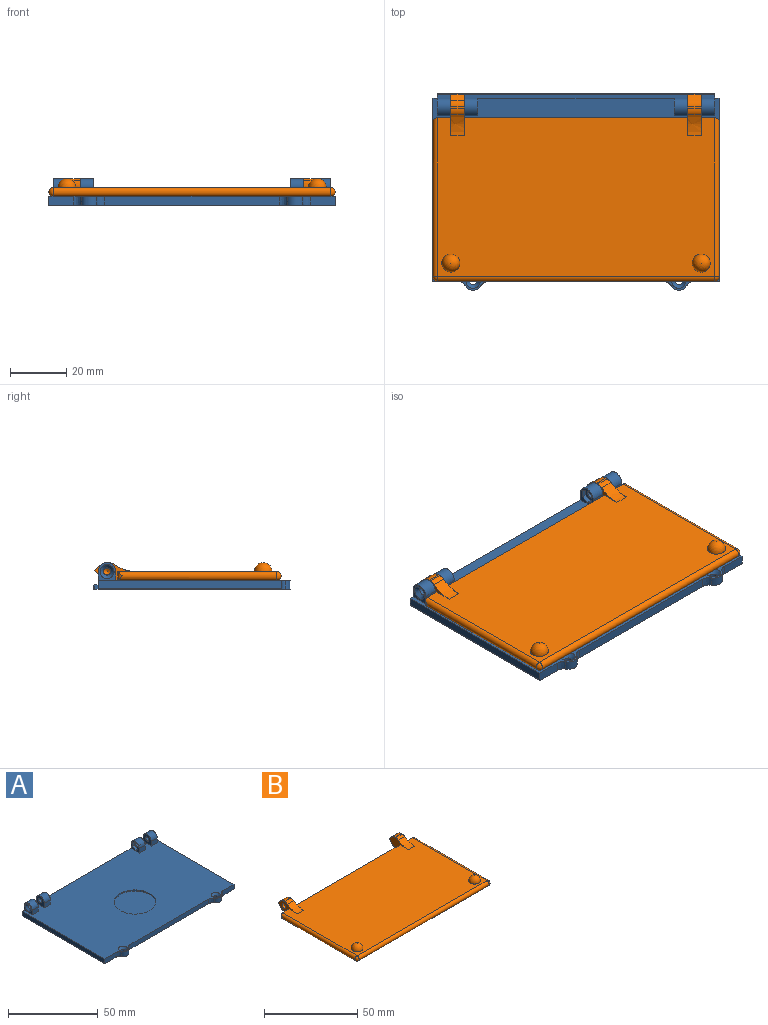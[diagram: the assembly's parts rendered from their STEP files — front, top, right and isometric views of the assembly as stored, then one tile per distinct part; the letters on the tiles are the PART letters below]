
ASSEMBLY  parts=2 mates=1
PART A: 66 faces, bbox 102x70.2x10.1 mm
  f0: plane 6.35x6.35mm, normal (-1,0,0), area 16.2mm2, adj f2,f11,f39,f41,f51,f52,f53,f54
  f1: plane 6.35x6.35mm, normal (1,0,0), area 16.2mm2, adj f2,f11,f34,f42,f44,f45,f46,f47
  f2: plane 101.97x68.62mm, normal (0,0,1), area 6061.6mm2, adj f0,f1,f3,f4,f5,f9,f10,f11
  f3: plane 8.8x3.18mm, normal (0,-1,0), area 27.9mm2, adj f2,f5,f8,f17,f29
  f4: plane 62x3.18mm, normal (0,-1,0), area 196.9mm2, adj f2,f8,f16,f18
  f5: plane 65.08x2.92mm, normal (1,0,0), area 190.1mm2, adj f2,f3,f11,f29
  f6: plane 97.94x1.09mm, normal (0,1,0), area 107mm2, adj f24,f25,f26,f27
  f7: plane 98.45x1.32mm, normal (0,0,1), area 130mm2, adj f11,f12,f13,f26
  f8: plane 101.46x69.94mm, normal (0,0,-1), area 6733.1mm2, adj f3,f4,f9,f11,f12,f13,f14,f15
  f9: plane 8.8x3.18mm, normal (0,-1,0), area 27.9mm2, adj f2,f8,f10,f19,f28
  f10: plane 65.08x2.92mm, normal (-1,0,0), area 190.1mm2, adj f2,f9,f11,f28
  f11: plane 101.6x6.35mm, normal (0,1,0), area 225.5mm2, adj f0,f1,f2,f5,f7,f8,f10,f12
  f12: plane 1.6x1.32mm, normal (1,0,0), area 2.1mm2, adj f7,f8,f11,f27
  f13: plane 1.6x1.32mm, normal (-1,0,0), area 2.1mm2, adj f7,f8,f11,f24
  f14: cylinder r=3.17mm len=5.5mm, axis (0,0,1), area 21.1mm2, adj f2,f8,f16,f17
  f15: cylinder r=3.17mm len=5.5mm, axis (0,0,-1), area 21.1mm2, adj f2,f8,f18,f19
  f16: bspline ~3.49x2.75mm, area 10.6mm2, adj f2,f4,f8,f14
  f17: bspline ~3.49x2.75mm, area 10.6mm2, adj f2,f3,f8,f14
  f18: bspline ~3.49x2.75mm, area 10.6mm2, adj f2,f4,f8,f15
  f19: bspline ~3.49x2.75mm, area 10.6mm2, adj f2,f8,f9,f15
  f20: cylinder r=1.27mm len=2.54mm, axis (0,0,1), area 14.2mm2, adj f8,f22
  f21: cylinder r=1.27mm len=2.54mm, axis (0,0,1), area 14.2mm2, adj f8,f23
  f22: cone r=1.27mm half-angle=41deg, axis (0,0,1), area 21.8mm2, adj f2,f20
  f23: cone r=1.27mm half-angle=41deg, axis (0,0,1), area 21.8mm2, adj f2,f21
  f24: cylinder r=0.25mm len=1.6mm, axis (0,0,-1), area 0.5mm2, adj f6,f13,f25,f26
  f25: cylinder r=0.25mm len=98.45mm, axis (1,0,0), area 39.2mm2, adj f6,f8,f24,f27
  f26: cylinder r=0.25mm len=98.45mm, axis (-1,0,0), area 39.2mm2, adj f6,f7,f24,f27
  f27: cylinder r=0.25mm len=1.6mm, axis (0,0,1), area 0.5mm2, adj f6,f12,f25,f26
  f28: cylinder r=0.25mm len=65.08mm, axis (0,1,0), area 26mm2, adj f8,f9,f10,f11
  f29: cylinder r=0.25mm len=65.08mm, axis (0,-1,0), area 26mm2, adj f3,f5,f8,f11
  f30: plane 6.35x6.35mm, normal (-1,0,0), area 16.6mm2, adj f2,f11,f31,f43,f63
  f31: plane 4.76x3.18mm, normal (0,-1,0), area 15.1mm2, adj f2,f30,f32,f43
  f32: plane 6.35x6.35mm, normal (1,0,0), area 30.9mm2, adj f2,f11,f31,f43,f61
  f33: plane 6.35x6.35mm, normal (-1,0,0), area 30.9mm2, adj f2,f11,f34,f42,f59
  f34: plane 4.76x3.18mm, normal (0,-1,0), area 15.1mm2, adj f1,f2,f33,f42
  f35: plane 6.35x6.35mm, normal (1,0,0), area 16.6mm2, adj f2,f11,f37,f40,f62
  f36: plane 6.35x6.35mm, normal (-1,0,0), area 30.9mm2, adj f2,f11,f37,f40,f60
  f37: plane 4.76x3.18mm, normal (0,-1,0), area 15.1mm2, adj f2,f35,f36,f40
  f38: plane 6.35x6.35mm, normal (1,0,0), area 30.9mm2, adj f2,f11,f39,f41,f58
  f39: plane 4.76x3.18mm, normal (0,-1,0), area 15.1mm2, adj f0,f2,f38,f41
  f40: cylinder r=3.17mm len=6.35mm, axis (-1,0,0), area 47.5mm2, adj f11,f35,f36,f37
  f41: cylinder r=3.17mm len=6.35mm, axis (-1,0,0), area 47.5mm2, adj f0,f11,f38,f39
  f42: cylinder r=3.17mm len=6.35mm, axis (-1,0,0), area 47.5mm2, adj f1,f11,f33,f34
  f43: cylinder r=3.17mm len=6.35mm, axis (-1,0,0), area 47.5mm2, adj f11,f30,f31,f32
  f44: plane 2.39x1.6mm, normal (0,0.5,-0.87), area 4.4mm2, adj f1,f45,f49,f50
  f45: plane 2.76x1.6mm, normal (0,1,0), area 4.4mm2, adj f1,f44,f46,f50
  f46: plane 2.39x1.6mm, normal (0,0.5,0.87), area 4.4mm2, adj f1,f45,f47,f50
  f47: plane 2.39x1.6mm, normal (0,-0.5,0.87), area 4.4mm2, adj f1,f46,f48,f50
  f48: plane 2.76x1.6mm, normal (0,-1,0), area 4.4mm2, adj f1,f47,f49,f50
  f49: plane 2.39x1.6mm, normal (0,-0.5,-0.87), area 4.4mm2, adj f1,f44,f48,f50
  f50: plane 5.51x4.78mm, normal (1,0,0), area 14.7mm2, adj f44,f45,f46,f47,f48,f49,f59
  f51: plane 2.39x1.59mm, normal (0,-0.5,-0.87), area 4.4mm2, adj f0,f52,f56,f57
  f52: plane 2.76x1.59mm, normal (0,-1,0), area 4.4mm2, adj f0,f51,f53,f57
  f53: plane 2.39x1.59mm, normal (0,-0.5,0.87), area 4.4mm2, adj f0,f52,f54,f57
  f54: plane 2.39x1.59mm, normal (0,0.5,0.87), area 4.4mm2, adj f0,f53,f55,f57
  f55: plane 2.76x1.59mm, normal (0,1,0), area 4.4mm2, adj f0,f54,f56,f57
  f56: plane 2.39x1.59mm, normal (0,0.5,-0.87), area 4.4mm2, adj f0,f51,f55,f57
  f57: plane 5.51x4.78mm, normal (-1,0,0), area 14.7mm2, adj f51,f52,f53,f54,f55,f56,f58
  f58: cylinder r=1.27mm len=3.18mm, axis (-1,0,0), area 25.3mm2, adj f38,f57
  f59: cylinder r=1.27mm len=3.16mm, axis (1,0,0), area 25.2mm2, adj f33,f50
  f60: cylinder r=1.27mm len=3.37mm, axis (1,0,0), area 26.9mm2, adj f36,f62
  f61: cylinder r=1.27mm len=3.37mm, axis (-1,0,0), area 26.9mm2, adj f32,f63
  f62: cone r=1.27mm half-angle=41deg, axis (1,0,0), area 21.8mm2, adj f35,f60
  f63: cone r=1.27mm half-angle=41deg, axis (-1,0,0), area 21.8mm2, adj f30,f61
  f64: cylinder r=11.63mm len=23.26mm, axis (0,0,1), area 57.9mm2, adj f2,f65
  f65: plane 23.26x23.26mm, normal (0,0,1), area 425mm2, adj f64
PART B: 36 faces, bbox 102.7x67.3x7.5 mm
  f0: cylinder r=3.17mm len=4.78mm, axis (-1,0,0), area 13.2mm2, adj f6,f9,f10,f22
  f1: cylinder r=3.17mm len=4.78mm, axis (-1,0,0), area 11.4mm2, adj f12,f13,f14,f19
  f2: plane 4.76x3.18mm, normal (0,1,0), area 15.1mm2, adj f5,f6,f13,f32
  f3: plane 79.35x3.18mm, normal (0,1,0), area 251.9mm2, adj f5,f6,f10,f12
  f4: plane 4.76x3.18mm, normal (0,1,0), area 15.1mm2, adj f5,f6,f9,f29
  f5: plane 98.43x56.36mm, normal (0,0,1), area 5422.8mm2, adj f2,f3,f4,f7,f8,f9,f10,f12
  f6: plane 98.43x60.18mm, normal (0,0,-1), area 5583.3mm2, adj f0,f2,f3,f4,f9,f10,f12,f13
  f7: sphere r=3.17mm, area 63.3mm2, adj f5
  f8: sphere r=3.17mm, area 63.3mm2, adj f5
  f9: plane 15.72x7.45mm, normal (1,0,0), area 37.5mm2, adj f0,f4,f5,f6,f11,f17,f18,f21
  f10: plane 15.72x7.45mm, normal (-1,0,0), area 43.8mm2, adj f0,f3,f5,f6,f11,f17,f18,f21
  f11: plane 4.78x0.65mm, normal (0,0,1), area 3.1mm2, adj f9,f10,f17,f18
  f12: plane 15.75x7.45mm, normal (1,0,0), area 43.9mm2, adj f1,f3,f5,f6,f14,f15,f16,f19
  f13: plane 15.75x7.45mm, normal (-1,0,0), area 37.6mm2, adj f1,f2,f5,f6,f14,f15,f16,f19
  f14: plane 4.78x0.65mm, normal (0,0,1), area 3.1mm2, adj f1,f12,f13,f16
  f15: cylinder r=3.17mm len=4.78mm, axis (-1,0,0), area 13.2mm2, adj f6,f12,f13,f20
  f16: cylinder r=3.17mm len=4.78mm, axis (1,0,0), area 9.8mm2, adj f12,f13,f14,f23
  f17: cylinder r=3.17mm len=4.78mm, axis (-1,0,0), area 13.1mm2, adj f9,f10,f11,f21
  f18: cylinder r=3.17mm len=4.78mm, axis (1,0,0), area 9.8mm2, adj f9,f10,f11,f24
  f19: plane 4.78x2.3mm, normal (0,0.64,0.77), area 14.3mm2, adj f1,f12,f13,f20
  f20: plane 4.78x2.43mm, normal (0,0.77,-0.64), area 15.1mm2, adj f12,f13,f15,f19
  f21: plane 4.78x2.03mm, normal (0,0.64,0.77), area 12.7mm2, adj f9,f10,f17,f22
  f22: plane 4.78x2.4mm, normal (0,0.77,-0.64), area 15mm2, adj f0,f9,f10,f21
  f23: bspline ~7.62x5.25mm, area 39.1mm2, adj f5,f12,f13,f16
  f24: bspline ~7.62x5.25mm, area 39.1mm2, adj f5,f9,f10,f18
  f25: cone r=0mm half-angle=59deg, axis (-1,0,0), area 7.4mm2, adj f26
  f26: cylinder r=1.42mm len=3.18mm, axis (-1,0,0), area 28.4mm2, adj f13,f25
  f27: cone r=0mm half-angle=59deg, axis (1,0,0), area 7.4mm2, adj f28
  f28: cylinder r=1.42mm len=3.18mm, axis (1,0,0), area 28.4mm2, adj f9,f27
  f29: cylinder r=1.59mm len=3.18mm, axis (0,0,1), area 4mm2, adj f4,f30
  f30: cylinder r=1.59mm len=56.36mm, axis (0,-1,0), area 277.1mm2, adj f5,f6,f29,f31
  f31: sphere r=1.59mm, area 7.9mm2, adj f30,f33
  f32: cylinder r=1.59mm len=3.18mm, axis (0,0,-1), area 4mm2, adj f2,f34
  f33: cylinder r=1.59mm len=98.43mm, axis (-1,0,0), area 490.9mm2, adj f5,f6,f31,f35
  f34: cylinder r=1.59mm len=56.36mm, axis (0,1,0), area 277.1mm2, adj f5,f6,f32,f35
  f35: sphere r=1.59mm, area 7.9mm2, adj f33,f34
PLACE A t=(0,2.53,-3.45)mm fixed
PLACE B rot(axis=(-1,0,0),0deg) t=(0,0.61,-0.27)mm
MATE revolute B.f0 <-> A.f41  axis (1,0,0) through (44.45,31.02,2.9)mm
